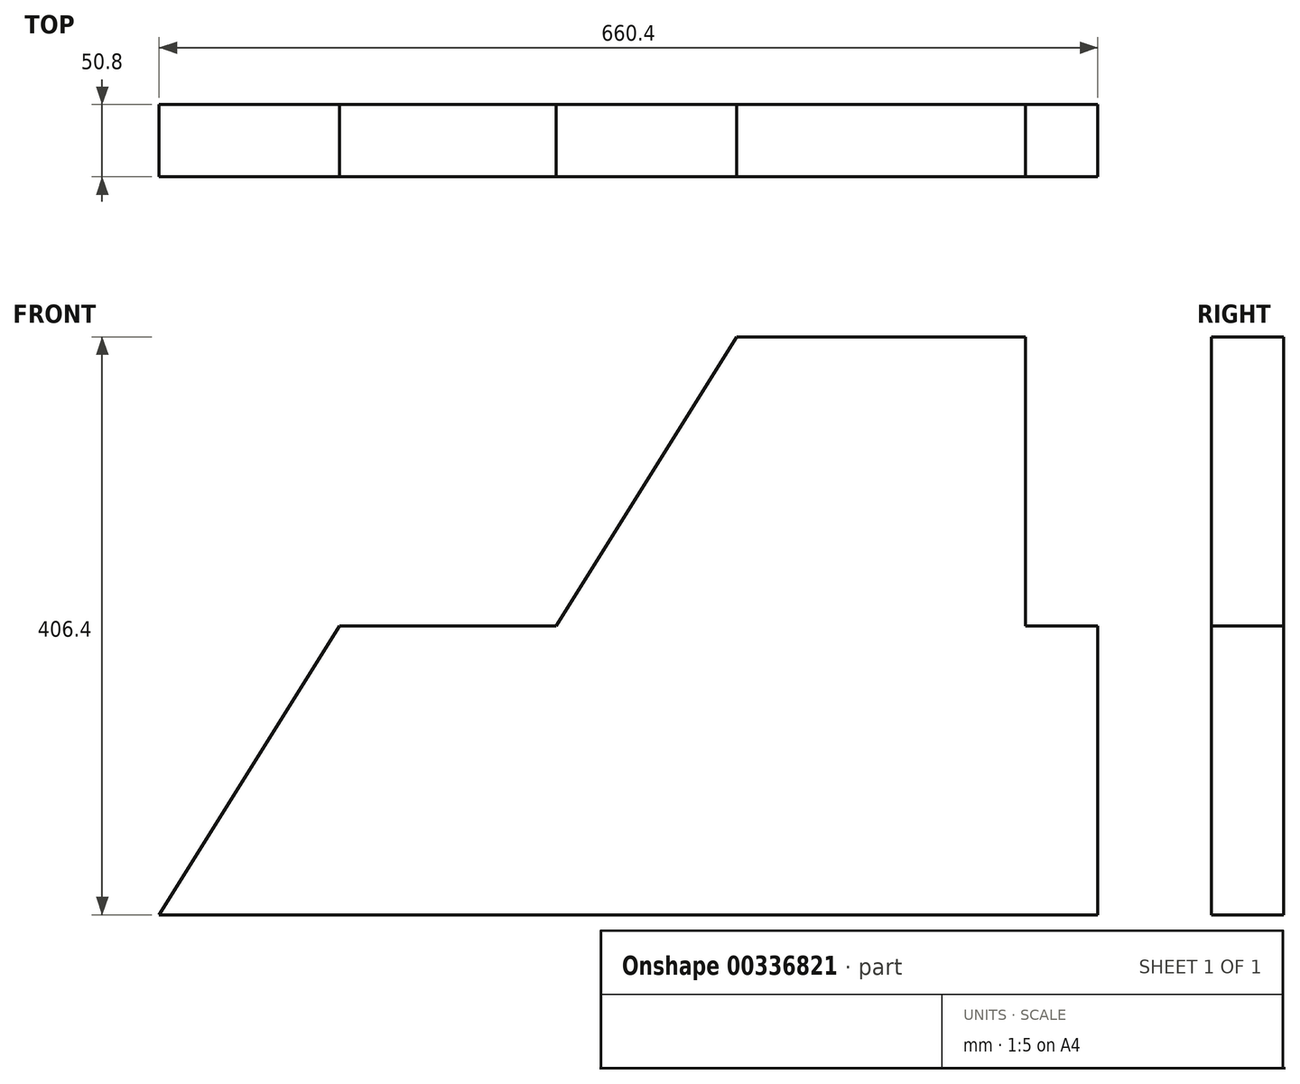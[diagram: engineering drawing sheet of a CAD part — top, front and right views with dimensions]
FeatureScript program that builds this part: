
annotation { "Feature Type Name" : "Feature", "Feature Type Description" : "" }
export const myFeature = defineFeature(function(context is Context, id is Id, definition is map)
    precondition{}
    {
        {
            var Q0;
            Q0=qCreatedBy(makeId("Front.planeOp"),FACE);
            var sketch = newSketch(context, id + "F0", { "sketchPlane" : qUnion([Q0])});
            skLineSegment(sketch, "E0", {"start": v(0, 0) * mm, "end": v(127, 203.2) * mm});
            skLineSegment(sketch, "E1", {"start": v(127, 203.2) * mm, "end": v(330.2, 203.2) * mm});
            skLineSegment(sketch, "E2", {"start": v(330.2, 203.2) * mm, "end": v(330.2, 0) * mm});
            skLineSegment(sketch, "E3", {"start": v(0, 0) * mm, "end": v(-152.4, 0) * mm});
            skLineSegment(sketch, "E4", {"start": v(-152.4, 0) * mm, "end": v(-279.4, -203.2) * mm});
            skLineSegment(sketch, "E5", {"start": v(-279.4, -203.2) * mm, "end": v(381, -203.2) * mm});
            skLineSegment(sketch, "E6", {"start": v(381, -203.2) * mm, "end": v(381, 0) * mm});
            skLineSegment(sketch, "E7", {"start": v(381, 0) * mm, "end": v(330.2, 0) * mm});
            skSolve(sketch);
        }
        {
            var Q0;
            Q0=makeQuery(id+"F0.imprint","IMPRINT",FACE,{"disambiguationData":[TD([[makeQuery(id+"F0.imprint","IMPRINT",EDGE,{"derivedFrom":sQuery(id+"F0.wireOp",EDGE,"E0")}),-1.0]])]});
            extrude(context, id + "F1", {"entities" : qUnion([Q0]), "depth" : 50.8 * mm});
        }
    });
